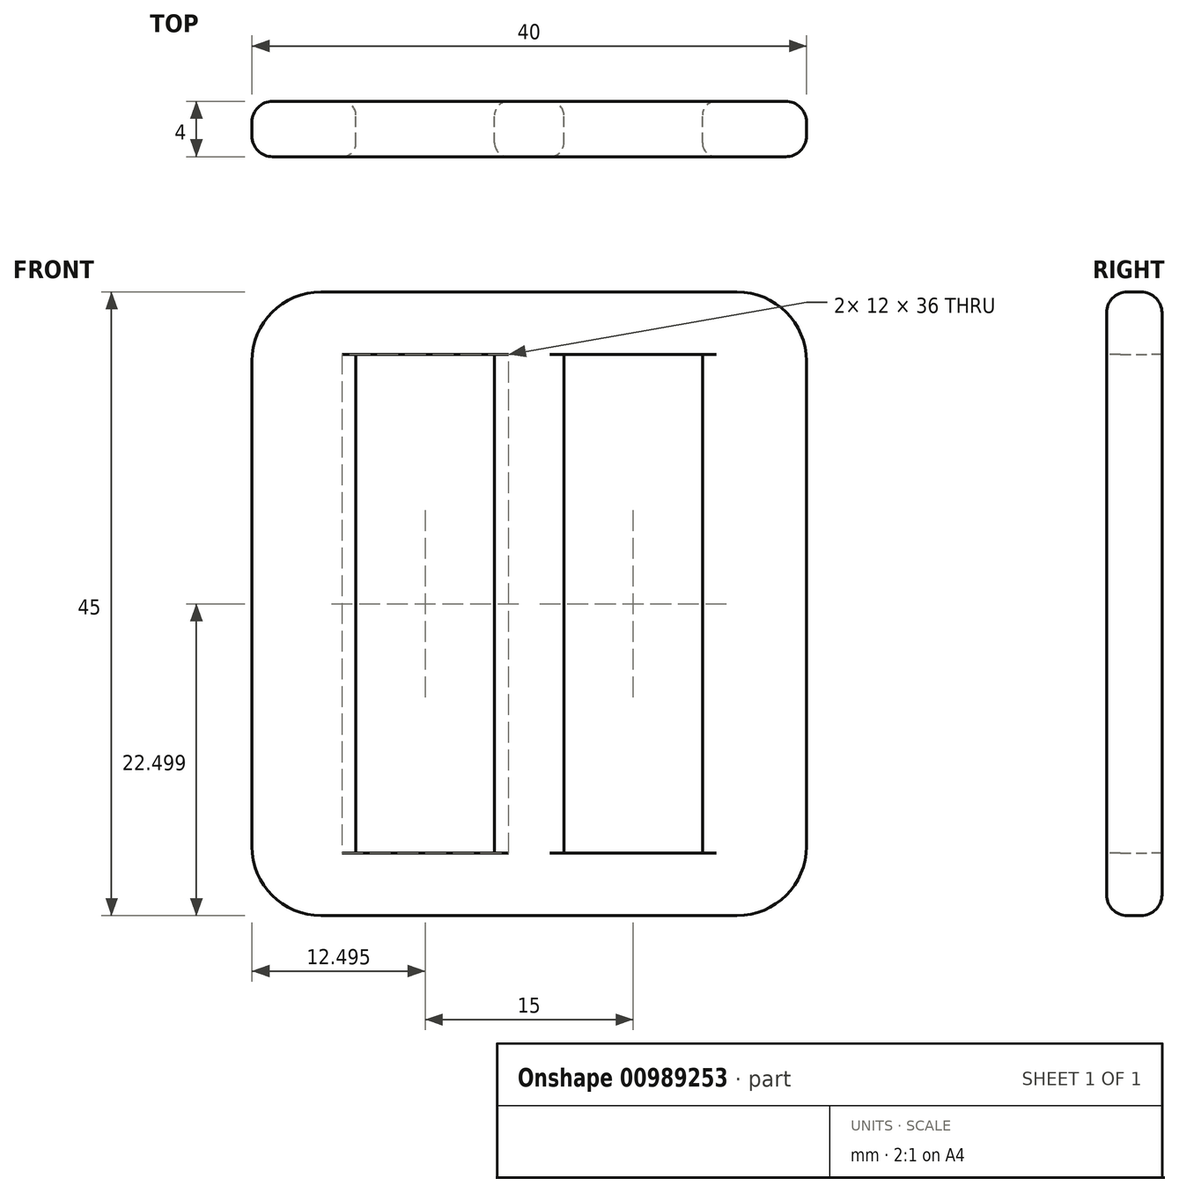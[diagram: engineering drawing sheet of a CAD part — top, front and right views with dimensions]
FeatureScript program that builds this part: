
annotation { "Feature Type Name" : "Feature", "Feature Type Description" : "" }
export const myFeature = defineFeature(function(context is Context, id is Id, definition is map)
    precondition{}
    {
        {
            var Q0;
            Q0=qCreatedBy(makeId("Front.planeOp"),FACE);
            var sketch = newSketch(context, id + "F0", { "sketchPlane" : qUnion([Q0])});
            skPoint(sketch, "E0.start.orphan", {"position": v(-18.13, 17.55) * mm});
            skPoint(sketch, "E1.start.orphan", {"position": v(-18.13, -18.45) * mm});
            skPoint(sketch, "E2.start.orphan", {"position": v(21.87, 17.55) * mm});
            skPoint(sketch, "E3.start.orphan", {"position": v(-18.13, -0.45) * mm});
            skPoint(sketch, "E4.trimOffspring.end.orphan", {"position": v(21.87, -0.45) * mm});
            skPoint(sketch, "E5.start.orphan", {"position": v(34.18, 17.55) * mm});
            skLineSegment(sketch, "E6", {"start": v(-10.63, 17.55) * mm, "end": v(-10.63, -18.45) * mm});
            skLineSegment(sketch, "E7", {"start": v(14.37, 17.55) * mm, "end": v(14.37, -18.45) * mm});
            skPoint(sketch, "E8.visualSharp", {"position": v(-18.13, 22.05) * mm});
            skPoint(sketch, "E9.visualSharp", {"position": v(21.87, 22.05) * mm});
            skPoint(sketch, "E10.visualSharp", {"position": v(21.87, -22.95) * mm});
            skPoint(sketch, "E11.visualSharp", {"position": v(-18.13, -22.95) * mm});
            skLineSegment(sketch, "E12", {"start": v(-13.13, -22.95) * mm, "end": v(16.87, -22.95) * mm});
            skLineSegment(sketch, "E13", {"start": v(-13.13, 22.05) * mm, "end": v(16.87, 22.05) * mm});
            skLineSegment(sketch, "E14", {"start": v(-18.13, 17.05) * mm, "end": v(-18.13, -17.95) * mm});
            skLineSegment(sketch, "E15", {"start": v(21.87, -17.95) * mm, "end": v(21.87, 17.05) * mm});
            skPoint(sketch, "E16.end.orphan", {"position": v(4.37, -18.45) * mm});
            skPoint(sketch, "E17.start.orphan", {"position": v(-5.63, -18.45) * mm});
            skLineSegment(sketch, "E18", {"start": v(-10.63, 17.55) * mm, "end": v(-0.63, 17.55) * mm});
            skLineSegment(sketch, "E19", {"start": v(-10.63, -18.45) * mm, "end": v(-0.63, -18.45) * mm});
            skLineSegment(sketch, "E20", {"start": v(-0.63, 17.55) * mm, "end": v(-0.63, -18.45) * mm});
            skLineSegment(sketch, "E21", {"start": v(14.37, -18.45) * mm, "end": v(4.37, -18.45) * mm});
            skLineSegment(sketch, "E22", {"start": v(4.37, 17.55) * mm, "end": v(14.37, 17.55) * mm});
            skLineSegment(sketch, "E23", {"start": v(4.37, 17.55) * mm, "end": v(4.37, -18.45) * mm});
            skArc(sketch, "E24.filletArc", {"start": v(-13.13, 22.05) * mm, "mid": v(-16.67, 20.58) * mm, "end": v(-18.13, 17.05) * mm});
            skArc(sketch, "E25.filletArc", {"start": v(21.87, 17.05) * mm, "mid": v(20.4, 20.58) * mm, "end": v(16.87, 22.05) * mm});
            skArc(sketch, "E26.filletArc", {"start": v(16.87, -22.95) * mm, "mid": v(20.4, -21.49) * mm, "end": v(21.87, -17.95) * mm});
            skArc(sketch, "E27.filletArc", {"start": v(-18.13, -17.95) * mm, "mid": v(-16.67, -21.49) * mm, "end": v(-13.13, -22.95) * mm});
            skSolve(sketch);
        }
        {
            var Q0;
            Q0=makeQuery(id+"F0.imprint","IMPRINT",FACE,{"disambiguationData":[TD([[makeQuery(id+"F0.imprint","IMPRINT",EDGE,{"derivedFrom":sQuery(id+"F0.wireOp",EDGE,"E6")}),-1.0]])]});
            extrude(context, id + "F1", {"entities" : qUnion([Q0]), "depth" : 4 * mm, "offsetDistance" : 25 * mm});
        }
        {
            var Q0;
            Q0=makeQuery(id+"F1.opExtrude","CAP_EDGE",EDGE,{"disambiguationData":[OSD([sQuery(id+"F0.wireOp",EDGE,"E20")])],"isStart":true});
            var Q1;
            Q1=makeQuery(id+"F1.opExtrude","CAP_EDGE",EDGE,{"disambiguationData":[OSD([sQuery(id+"F0.wireOp",EDGE,"E23")])],"isStart":true});
            var Q2;
            Q2=makeQuery(id+"F1.opExtrude","CAP_EDGE",EDGE,{"disambiguationData":[OSD([sQuery(id+"F0.wireOp",EDGE,"E23")])],"isStart":false});
            var Q3;
            Q3=makeQuery(id+"F1.opExtrude","CAP_EDGE",EDGE,{"disambiguationData":[OSD([sQuery(id+"F0.wireOp",EDGE,"E20")])],"isStart":false});
            fillet(context, id + "F2", {"entities" : qUnion([Q0, Q1, Q2, Q3]), "radius" : 1 * mm, "tangentPropagation" : true, "allowEdgeOverflow" : false});
        }
        {
            var Q0;
            Q0=makeQuery(id+"F1.opExtrude","CAP_EDGE",EDGE,{"disambiguationData":[OSD([sQuery(id+"F0.wireOp",EDGE,"E7")])],"isStart":false});
            var Q1;
            Q1=makeQuery(id+"F1.opExtrude","CAP_EDGE",EDGE,{"disambiguationData":[OSD([sQuery(id+"F0.wireOp",EDGE,"E7")])],"isStart":true});
            var Q2;
            Q2=makeQuery(id+"F1.opExtrude","CAP_EDGE",EDGE,{"disambiguationData":[OSD([sQuery(id+"F0.wireOp",EDGE,"E6")])],"isStart":false});
            var Q3;
            Q3=makeQuery(id+"F1.opExtrude","CAP_EDGE",EDGE,{"disambiguationData":[OSD([sQuery(id+"F0.wireOp",EDGE,"E6")])],"isStart":true});
            fillet(context, id + "F3", {"entities" : qUnion([Q0, Q1, Q2, Q3]), "radius" : 1 * mm, "tangentPropagation" : true, "allowEdgeOverflow" : false});
        }
        {
            var Q0;
            Q0=makeQuery(id+"F1.opExtrude","CAP_EDGE",EDGE,{"disambiguationData":[OSD([sQuery(id+"F0.wireOp",EDGE,"E15")])],"isStart":false});
            var Q1;
            Q1=makeQuery(id+"F1.opExtrude","CAP_EDGE",EDGE,{"disambiguationData":[OSD([sQuery(id+"F0.wireOp",EDGE,"E15")])],"isStart":true});
            fillet(context, id + "F4", {"entities" : qUnion([Q0, Q1]), "radius" : 1.5 * mm, "tangentPropagation" : true, "allowEdgeOverflow" : false});
        }
    });
